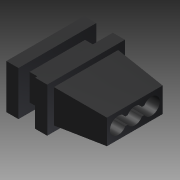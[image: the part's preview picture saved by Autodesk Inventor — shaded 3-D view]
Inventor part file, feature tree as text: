
AUTODESK INVENTOR PART (.ipt)
format: ipt  version: 2013 (Build 170138000, 138)  size: 123,392 bytes
history: native  units: in
note: dims shown in document units (in); Inventor stores cm internally (conversion verified against a paired STEP export)
features: extrude x4, sketch x4, pattern_linear x1, projected_geometry x1
ambient origin geometry x8: Origin, YZ Plane, XZ Plane, XY Plane, X Axis, Y Axis, Z Axis, Center Point
bodies: Solid1 (feature_tree)
feature tree (10):
  extrude  "Extrusion1"  Depth=0.157in
  extrude  "Extrusion2"  Depth=0.197in
  pattern_linear  "Rectangular Pattern1"  Count1=2 Spacing1=0.102in
  extrude  "Extrusion3"  Depth=0.173in
  extrude  "Extrusion4"  Depth=0.228in
  sketch  "Sketch1"  dims[d0=0.276in d1=0.157in]
  sketch  "Sketch2"  dims[d2=0.043in d3=0.0in d4=0.197in]
  sketch  "Sketch3"  dims[d5=0.094in]
  sketch  "Sketch4"  dims[d6=0.059in d7=0.0in d8=0.7874in d10=0.102in d11=0.173in d12=-0.0344in d14=0.228in d15=0.118in d16=0.173in d17=0.0in]
  projected_geometry  "Projected Loop1"
